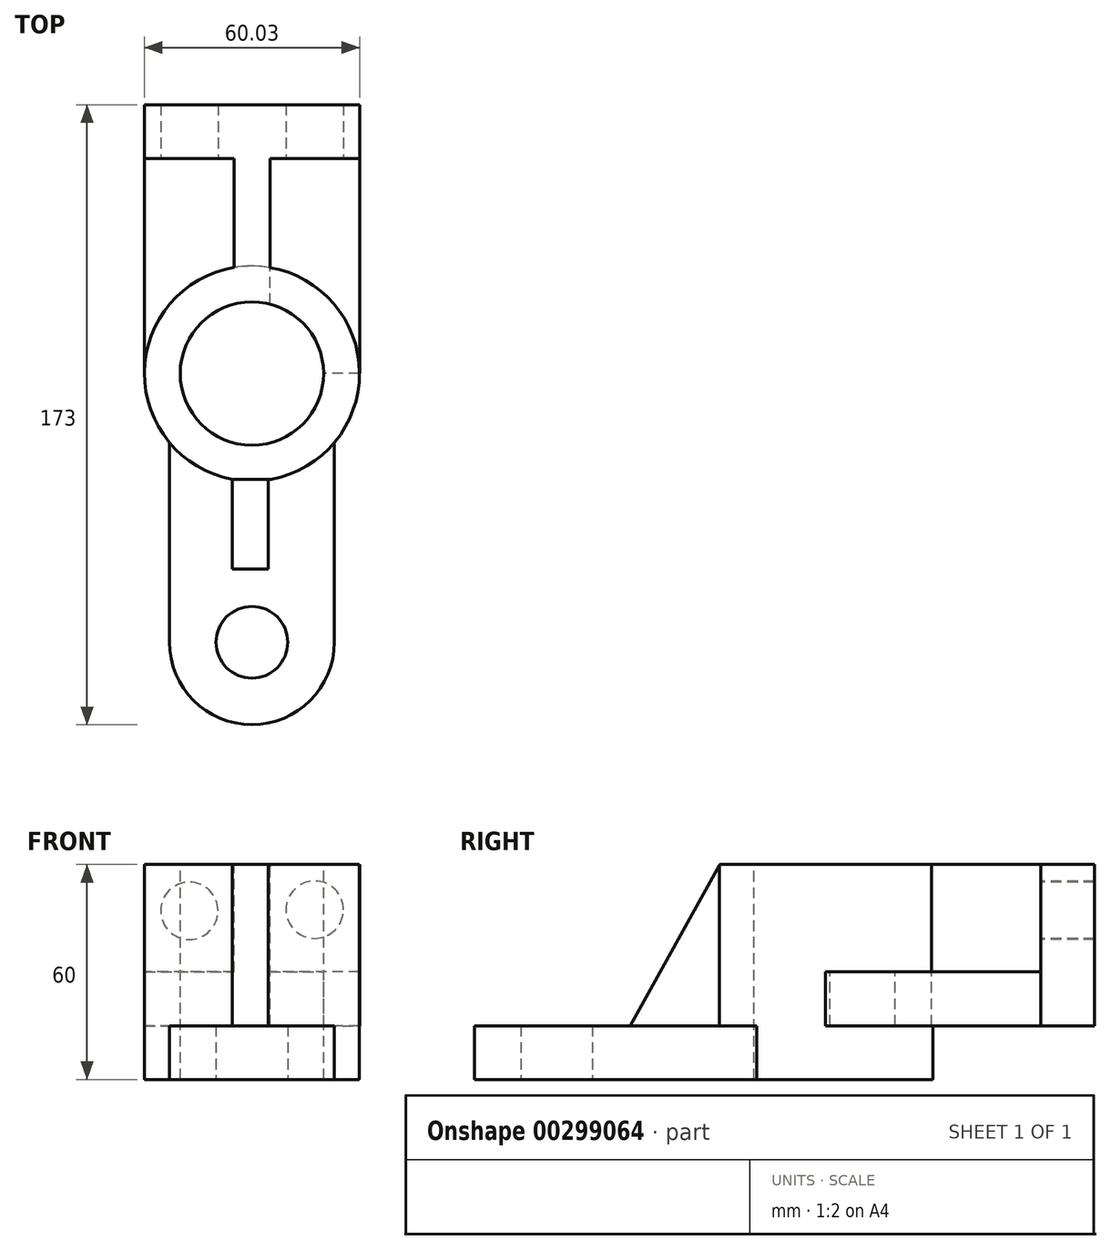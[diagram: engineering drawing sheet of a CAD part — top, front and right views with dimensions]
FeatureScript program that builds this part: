
annotation { "Feature Type Name" : "Feature", "Feature Type Description" : "" }
export const myFeature = defineFeature(function(context is Context, id is Id, definition is map)
    precondition{}
    {
        {
            var Q0;
            Q0=qCreatedBy(makeId("Top.planeOp"),FACE);
            var sketch = newSketch(context, id + "F0", { "sketchPlane" : qUnion([Q0])});
            skCircle(sketch, "E0", {"center": v(0, 0) * mm, "radius": 20 * mm});
            skCircle(sketch, "E1", {"center": v(0, 0) * mm, "radius": 30 * mm});
            skPoint(sketch, "E2.start.orphan", {"position": v(27.9, 50) * mm});
            skLineSegment(sketch, "E3", {"start": v(-4.97, 29.58) * mm, "end": v(-4.97, 60) * mm});
            skLineSegment(sketch, "E4", {"start": v(5.03, 29.58) * mm, "end": v(5.03, 60) * mm});
            skLineSegment(sketch, "E5", {"start": v(-4.97, 60) * mm, "end": v(-29.97, 60) * mm});
            skLineSegment(sketch, "E6", {"start": v(-29.97, 60) * mm, "end": v(-29.97, 75) * mm});
            skLineSegment(sketch, "E7", {"start": v(-29.97, 75) * mm, "end": v(30.03, 75) * mm});
            skLineSegment(sketch, "E8", {"start": v(30.03, 75) * mm, "end": v(30.03, 60) * mm});
            skLineSegment(sketch, "E9", {"start": v(30.03, 60) * mm, "end": v(5.03, 60) * mm});
            skSolve(sketch);
        }
        {
            var Q0;
            Q0=makeQuery(id+"F0.imprint","IMPRINT",FACE,{"disambiguationData":[TD([[makeQuery(id+"F0.imprint","IMPRINT",EDGE,{"derivedFrom":sQuery(id+"F0.wireOp",EDGE,"E0")}),-1.0]])]});
            extrude(context, id + "F1", {"entities" : qUnion([Q0]), "oppositeDirection" : true, "depth" : 60 * mm});
        }
        {
            var Q0;
            {var subQ1=sQuery(id+"F0.wireOp",EDGE,"E3");Q0=makeQuery(id+"F0.imprint","IMPRINT",FACE,{"disambiguationData":[TD([[makeQuery(id+"F0.imprint","IMPRINT",EDGE,{"derivedFrom":subQ1}),-1.0]])]});}
            extrude(context, id + "F2", {"entities" : qUnion([Q0]), "oppositeDirection" : true, "depth" : 45 * mm});
        }
        {
            var Q0;
            Q0=makeQuery(id+"F2.opExtrude","SWEPT_FACE",FACE,{"disambiguationData":[OSD([sQuery(id+"F0.wireOp",EDGE,"E5")])]});
            var sketch = newSketch(context, id + "F3", { "sketchPlane" : qUnion([Q0])});
            skCircle(sketch, "E10", {"center": v(-17.47, -12.93) * mm, "radius": 8 * mm});
            skPoint(sketch, "E10.centerSnap0", {"position": v(-17.47, 0) * mm});
            skPoint(sketch, "E11.0", {"position": v(17.53, 0) * mm});
            skCircle(sketch, "E12", {"center": v(17.53, -12.62) * mm, "radius": 8 * mm});
            skSolve(sketch);
        }
        {
            var Q0;
            Q0=makeQuery(id+"F3.imprint","IMPRINT",FACE,{"disambiguationData":[TD([[makeQuery(id+"F3.imprint","IMPRINT",EDGE,{"derivedFrom":sQuery(id+"F3.wireOp",EDGE,"E10")}),1.0]])]});
            var Q1;
            Q1=makeQuery(id+"F3.imprint","IMPRINT",FACE,{"disambiguationData":[TD([[makeQuery(id+"F3.imprint","IMPRINT",EDGE,{"derivedFrom":sQuery(id+"F3.wireOp",EDGE,"E12")}),1.0]])]});
            extrude(context, id + "F4", {"entities" : qUnion([Q0, Q1]), "operationType" : NewBodyOperationType.REMOVE, "oppositeDirection" : true, "depth" : 25 * mm});
        }
        {
            var Q0;
            Q0=makeQuery(id+"F1.opExtrude","CAP_FACE",FACE,{"disambiguationData":[OSD([sQuery(id+"F0.wireOp",EDGE,"E0"),sQuery(id+"F0.wireOp",EDGE,"E1")])],"isStart":false});
            var sketch = newSketch(context, id + "F5", { "sketchPlane" : qUnion([Q0])});
            skLineSegment(sketch, "E13", {"start": v(0, 0) * mm, "end": v(0, 75) * mm});
            skLineSegment(sketch, "E14", {"start": v(-23, 19.26) * mm, "end": v(-23, 75) * mm});
            skLineSegment(sketch, "E15", {"start": v(23, 19.26) * mm, "end": v(23, 75) * mm});
            skArc(sketch, "E16", {"start": v(23, 75) * mm, "mid": v(0, 98) * mm, "end": v(-23, 75) * mm});
            skCircle(sketch, "E17", {"center": v(0, 75) * mm, "radius": 10 * mm});
            skSolve(sketch);
        }
        {
            var Q0;
            {var subQ1=sQuery(id+"F5.wireOp",EDGE,"E14");Q0=makeQuery(id+"F5.imprint","IMPRINT",FACE,{"disambiguationData":[TD([[makeQuery(id+"F5.imprint","IMPRINT",EDGE,{"derivedFrom":subQ1}),-1.0]])]});}
            extrude(context, id + "F6", {"entities" : qUnion([Q0]), "operationType" : NewBodyOperationType.ADD, "oppositeDirection" : true, "depth" : 15 * mm});
        }
        {
            var Q0;
            Q0=qCreatedBy(makeId("Top.planeOp"),FACE);
            var sketch = newSketch(context, id + "F7", { "sketchPlane" : qUnion([Q0])});
            skCircle(sketch, "E18.0", {"center": v(0, 0) * mm, "radius": 30 * mm});
            skLineSegment(sketch, "E19", {"start": v(0, 0) * mm, "end": v(0, -75) * mm, "construction": true});
            skLineSegment(sketch, "E20", {"start": v(4.52, -29.66) * mm, "end": v(4.52, -54.5) * mm});
            skLineSegment(sketch, "E21", {"start": v(4.52, -54.5) * mm, "end": v(-5.48, -54.5) * mm});
            skLineSegment(sketch, "E22", {"start": v(-5.48, -54.5) * mm, "end": v(-5.48, -29.5) * mm});
            skSolve(sketch);
        }
        {
            var Q0;
            {var subQ0=sQuery(id+"F7.wireOp",EDGE,"E20");Q0=makeQuery(id+"F7.imprint","IMPRINT",FACE,{"disambiguationData":[TD([[makeQuery(id+"F7.imprint","IMPRINT",EDGE,{"derivedFrom":subQ0}),-1.0]])]});}
            extrude(context, id + "F8", {"entities" : qUnion([Q0]), "operationType" : NewBodyOperationType.ADD, "oppositeDirection" : true, "depth" : 45 * mm});
        }
        {
            var Q0;
            Q0=makeQuery(id+"F8.opExtrude","SWEPT_FACE",FACE,{"disambiguationData":[OSD([sQuery(id+"F7.wireOp",EDGE,"E22")])]});
            var sketch = newSketch(context, id + "F9", { "sketchPlane" : qUnion([Q0])});
            skLineSegment(sketch, "E23", {"start": v(29.5, 0) * mm, "end": v(54.5, -45) * mm});
            skLineSegment(sketch, "E24", {"start": v(29.5, 0) * mm, "end": v(54.5, 0) * mm});
            skLineSegment(sketch, "E25", {"start": v(54.5, 0) * mm, "end": v(54.5, -45) * mm});
            skSolve(sketch);
        }
        {
            var Q0;
            Q0=makeQuery(id+"F9.imprint","IMPRINT",FACE,{"disambiguationData":[TD([[makeQuery(id+"F9.imprint","IMPRINT",EDGE,{"derivedFrom":sQuery(id+"F9.wireOp",EDGE,"E23")}),1.0]])]});
            extrude(context, id + "F10", {"entities" : qUnion([Q0]), "operationType" : NewBodyOperationType.REMOVE, "oppositeDirection" : true, "depth" : 25 * mm});
        }
        {
            var Q0;
            Q0=makeQuery(id+"F2.opExtrude","SWEPT_FACE",FACE,{"disambiguationData":[OSD([sQuery(id+"F0.wireOp",EDGE,"E5")])]});
            var sketch = newSketch(context, id + "F11", { "sketchPlane" : qUnion([Q0])});
            skLineSegment(sketch, "E26", {"start": v(-29.97, -45) * mm, "end": v(-29.97, -30) * mm});
            skLineSegment(sketch, "E27", {"start": v(-29.97, -30) * mm, "end": v(-4.97, -30) * mm});
            skLineSegment(sketch, "E28", {"start": v(-4.97, -30) * mm, "end": v(-4.97, -45) * mm});
            skLineSegment(sketch, "E29", {"start": v(-4.97, -45) * mm, "end": v(-29.97, -45) * mm});
            skSolve(sketch);
        }
        {
            var Q0;
            Q0=makeQuery(id+"F11.imprint","IMPRINT",FACE,{"disambiguationData":[TD([[makeQuery(id+"F11.imprint","IMPRINT",EDGE,{"derivedFrom":sQuery(id+"F11.wireOp",EDGE,"E26")}),-1.0]])]});
            extrude(context, id + "F12", {"entities" : qUnion([Q0]), "operationType" : NewBodyOperationType.ADD, "depth" : 60 * mm});
        }
        {
            var Q0;
            Q0=makeQuery(id+"F2.opExtrude","SWEPT_FACE",FACE,{"disambiguationData":[OSD([sQuery(id+"F0.wireOp",EDGE,"E9")])]});
            var sketch = newSketch(context, id + "F13", { "sketchPlane" : qUnion([Q0])});
            skLineSegment(sketch, "E30", {"start": v(30.03, -45) * mm, "end": v(30.03, -30) * mm});
            skLineSegment(sketch, "E31", {"start": v(30.03, -30) * mm, "end": v(5.03, -30) * mm});
            skLineSegment(sketch, "E32", {"start": v(5.03, -30) * mm, "end": v(5.03, -45) * mm});
            skLineSegment(sketch, "E33", {"start": v(5.03, -45) * mm, "end": v(30.03, -45) * mm});
            skSolve(sketch);
        }
        {
            var Q0;
            Q0 = qSketchRegion(id + "F13", true);
            extrude(context, id + "F14", {"entities" : qUnion([Q0]), "depth" : 60 * mm});
        }
        {
            var Q0;
            Q0=makeQuery(id+"F0.imprint","IMPRINT",FACE,{"disambiguationData":[TD([[makeQuery(id+"F0.imprint","IMPRINT",EDGE,{"derivedFrom":sQuery(id+"F0.wireOp",EDGE,"E0")}),1.0]])]});
            extrude(context, id + "F15", {"entities" : qUnion([Q0]), "operationType" : NewBodyOperationType.REMOVE, "endBound" : BoundingType.THROUGH_ALL, "oppositeDirection" : true, "depth" : 25 * mm});
        }
    });
